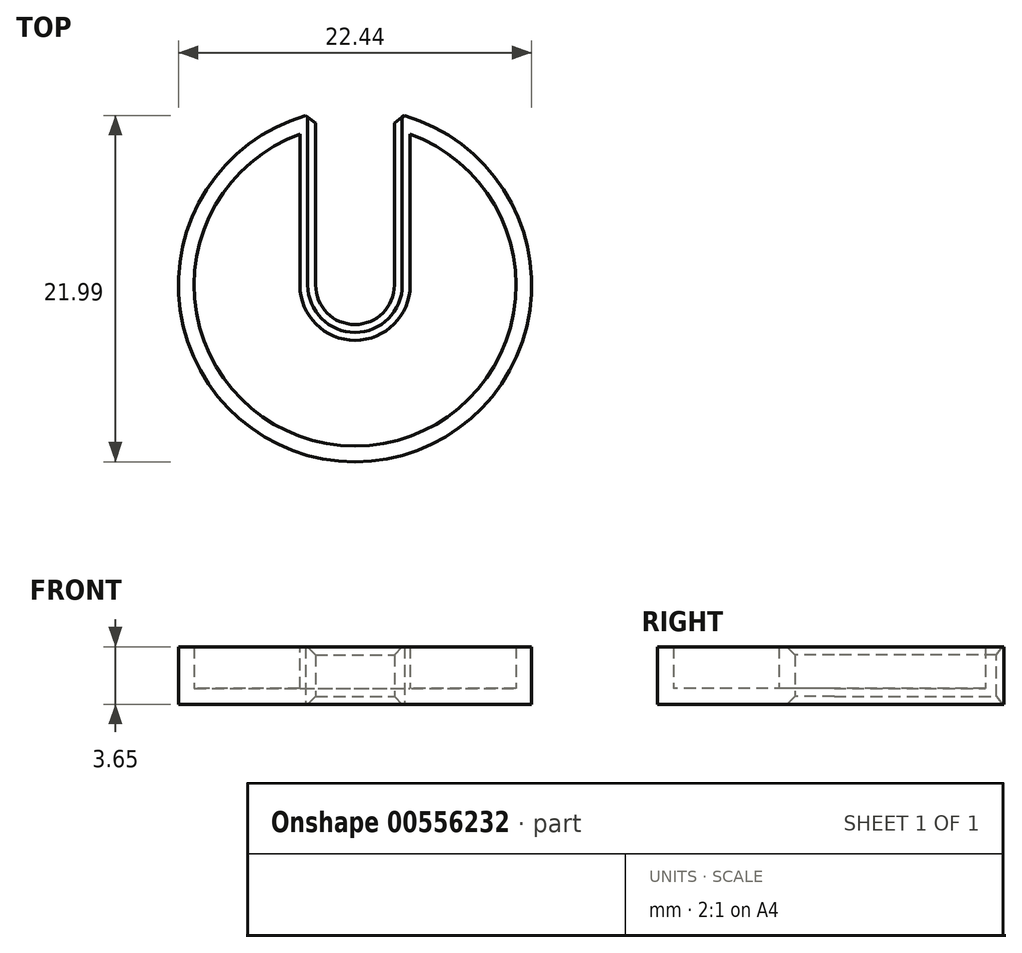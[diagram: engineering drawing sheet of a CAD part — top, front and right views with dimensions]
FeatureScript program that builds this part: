
annotation { "Feature Type Name" : "Feature", "Feature Type Description" : "" }
export const myFeature = defineFeature(function(context is Context, id is Id, definition is map)
    precondition{}
    {
        {
            var Q0;
            Q0=qCreatedBy(makeId("Top.planeOp"),FACE);
            var sketch = newSketch(context, id + "F0", { "sketchPlane" : qUnion([Q0])});
            skCircle(sketch, "E0", {"center": v(0, 0) * mm, "radius": 11.22 * mm});
            skCircle(sketch, "E1", {"center": v(0, 0) * mm, "radius": 2.5 * mm});
            skLineSegment(sketch, "E2", {"start": v(-2.5, 0) * mm, "end": v(2.5, 0) * mm});
            skLineSegment(sketch, "E3", {"start": v(-2.5, 0) * mm, "end": v(-2.5, 10.94) * mm});
            skLineSegment(sketch, "E4", {"start": v(2.5, 0) * mm, "end": v(2.5, 10.94) * mm});
            skSolve(sketch);
        }
        {
            var Q0;
            {var subQ0=sQuery(id+"F0.wireOp",EDGE,"E3");Q0=makeQuery(id+"F0.imprint","IMPRINT",FACE,{"disambiguationData":[TD([[makeQuery(id+"F0.imprint","IMPRINT",EDGE,{"derivedFrom":subQ0}),1.0]])]});}
            extrude(context, id + "F1", {"entities" : qUnion([Q0]), "depth" : 3.65 * mm, "offsetDistance" : 25 * mm});
        }
        {
            var Q0;
            Q0=makeQuery(id+"F1.opExtrude","CAP_FACE",FACE,{"disambiguationData":[OSD([sQuery(id+"F0.wireOp",EDGE,"E0"),sQuery(id+"F0.wireOp",EDGE,"E1"),sQuery(id+"F0.wireOp",EDGE,"E3"),sQuery(id+"F0.wireOp",EDGE,"E4")])],"isStart":false});
            shell(context, id + "F2", {"entities" : qUnion([Q0]), "thickness" : 1 * mm});
        }
        {
            var Q0;
            Q0=makeQuery(id+"F1.opExtrude","CAP_EDGE",EDGE,{"disambiguationData":[OSD([sQuery(id+"F0.wireOp",EDGE,"E1")])],"isStart":false});
            var Q1;
            Q1=makeQuery(id+"F1.opExtrude","CAP_EDGE",EDGE,{"disambiguationData":[OSD([sQuery(id+"F0.wireOp",EDGE,"E1")])],"isStart":true});
            var Q2;
            Q2=makeQuery(id+"F1.opExtrude","SWEPT_EDGE",EDGE,{"disambiguationData":[OSD([sQuery(id+"F0.wireOp",EDGE,"E0"),sQuery(id+"F0.wireOp",EDGE,"E3")])]});
            var Q3;
            Q3=makeQuery(id+"F1.opExtrude","SWEPT_EDGE",EDGE,{"disambiguationData":[OSD([sQuery(id+"F0.wireOp",EDGE,"E0"),sQuery(id+"F0.wireOp",EDGE,"E4")])]});
            chamfer(context, id + "F3", {"entities" : qUnion([Q0, Q1, Q2, Q3]), "width" : 0.5 * mm, "tangentPropagation" : true});
        }
    });
